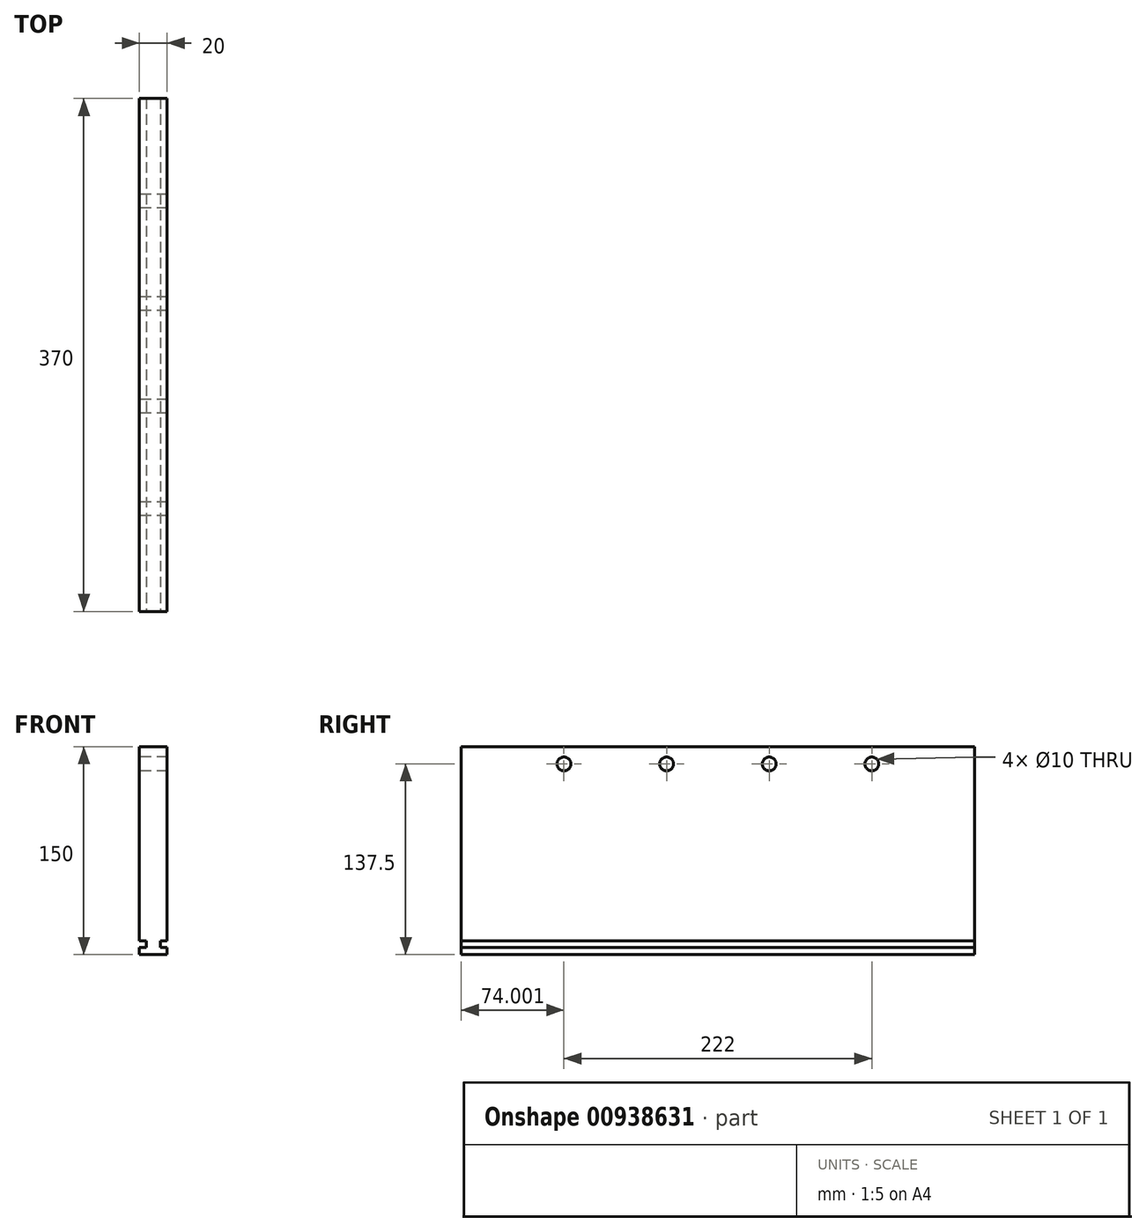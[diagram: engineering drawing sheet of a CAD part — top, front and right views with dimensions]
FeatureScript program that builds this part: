
annotation { "Feature Type Name" : "Feature", "Feature Type Description" : "" }
export const myFeature = defineFeature(function(context is Context, id is Id, definition is map)
    precondition{}
    {
        {
            var Q0;
            Q0=qCreatedBy(makeId("Right.planeOp"),FACE);
            var sketch = newSketch(context, id + "F0", { "sketchPlane" : qUnion([Q0])});
            skLineSegment(sketch, "E0.bottom", {"start": v(-199.06, 41.19) * mm, "end": v(170.94, 41.19) * mm});
            skLineSegment(sketch, "E0.top", {"start": v(-199.06, -108.81) * mm, "end": v(170.94, -108.81) * mm});
            skLineSegment(sketch, "E0.left", {"start": v(-199.06, 41.19) * mm, "end": v(-199.06, -108.81) * mm});
            skLineSegment(sketch, "E0.right", {"start": v(170.94, 41.19) * mm, "end": v(170.94, -108.81) * mm});
            skCircle(sketch, "E1", {"center": v(-125.06, 28.69) * mm, "radius": 5 * mm});
            skCircle(sketch, "E2", {"center": v(-51.06, 28.69) * mm, "radius": 5 * mm});
            skCircle(sketch, "E3", {"center": v(22.94, 28.69) * mm, "radius": 5 * mm});
            skCircle(sketch, "E4", {"center": v(96.94, 28.69) * mm, "radius": 5 * mm});
            skSolve(sketch);
        }
        {
            var Q0;
            Q0=makeQuery(id+"F0.imprint","IMPRINT",FACE,{"disambiguationData":[TD([[makeQuery(id+"F0.imprint","IMPRINT",EDGE,{"derivedFrom":sQuery(id+"F0.wireOp",EDGE,"E0.bottom")}),-1.0]])]});
            extrude(context, id + "F1", {"entities" : qUnion([Q0]), "depth" : 10 * mm, "offsetDistance" : 25 * mm});
        }
        {
            var Q0;
            Q0=makeQuery(id+"F1.opExtrude","CAP_FACE",FACE,{"disambiguationData":[OSD([sQuery(id+"F0.wireOp",EDGE,"E0.bottom"),sQuery(id+"F0.wireOp",EDGE,"E0.top"),sQuery(id+"F0.wireOp",EDGE,"E0.left"),sQuery(id+"F0.wireOp",EDGE,"E0.right"),sQuery(id+"F0.wireOp",EDGE,"E1"),sQuery(id+"F0.wireOp",EDGE,"E2"),sQuery(id+"F0.wireOp",EDGE,"E3"),sQuery(id+"F0.wireOp",EDGE,"E4")])],"isStart":true});
            var sketch = newSketch(context, id + "F2", { "sketchPlane" : qUnion([Q0])});
            skLineSegment(sketch, "E5.bottom", {"start": v(-170.94, -98.81) * mm, "end": v(199.06, -98.81) * mm});
            skLineSegment(sketch, "E5.top", {"start": v(-170.94, -103.81) * mm, "end": v(199.06, -103.81) * mm});
            skLineSegment(sketch, "E5.left", {"start": v(-170.94, -98.81) * mm, "end": v(-170.94, -103.81) * mm});
            skLineSegment(sketch, "E5.right", {"start": v(199.06, -98.81) * mm, "end": v(199.06, -103.81) * mm});
            skSolve(sketch);
        }
        {
            var Q0;
            Q0=makeQuery(id+"F2.imprint","IMPRINT",FACE,{"disambiguationData":[TD([[makeQuery(id+"F2.imprint","IMPRINT",EDGE,{"derivedFrom":sQuery(id+"F2.wireOp",EDGE,"E5.bottom")}),-1.0]])]});
            extrude(context, id + "F3", {"entities" : qUnion([Q0]), "operationType" : NewBodyOperationType.REMOVE, "oppositeDirection" : true, "depth" : 5 * mm, "offsetDistance" : 25 * mm});
        }
        {
            var Q0;
            Q0=makeQuery(id+"F1.opExtrude","SWEPT_BODY",BODY,{"disambiguationData":[OSD([sQuery(id+"F0.wireOp",EDGE,"E0.bottom"),sQuery(id+"F0.wireOp",EDGE,"E0.top"),sQuery(id+"F0.wireOp",EDGE,"E0.left"),sQuery(id+"F0.wireOp",EDGE,"E0.right"),sQuery(id+"F0.wireOp",EDGE,"E1"),sQuery(id+"F0.wireOp",EDGE,"E2"),sQuery(id+"F0.wireOp",EDGE,"E3"),sQuery(id+"F0.wireOp",EDGE,"E4")])]});
            var Q1;
            Q1=makeQuery(id+"F1.opExtrude","CAP_FACE",FACE,{"disambiguationData":[OSD([sQuery(id+"F0.wireOp",EDGE,"E0.bottom"),sQuery(id+"F0.wireOp",EDGE,"E0.top"),sQuery(id+"F0.wireOp",EDGE,"E0.left"),sQuery(id+"F0.wireOp",EDGE,"E0.right"),sQuery(id+"F0.wireOp",EDGE,"E1"),sQuery(id+"F0.wireOp",EDGE,"E2"),sQuery(id+"F0.wireOp",EDGE,"E3"),sQuery(id+"F0.wireOp",EDGE,"E4")])],"isStart":false});
            mirror(context, id + "F4", {"operationType" : NewBodyOperationType.ADD, "entities" : qUnion([Q0]), "mirrorPlane" : qUnion([Q1])});
        }
    });
